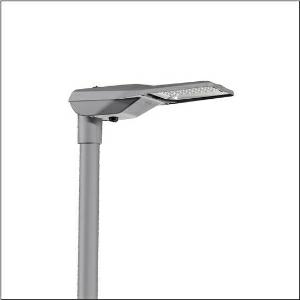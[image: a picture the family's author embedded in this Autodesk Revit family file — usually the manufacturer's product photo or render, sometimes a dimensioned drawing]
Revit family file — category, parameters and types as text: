
# Revit family: streetlight_sl_21_iq_mini___st1_0a_5xe2d61y08gb_62ef
name_source: partatom
category: Lighting Fixtures
units: mm (PartAtom-declared; Revit-internal decimal feet)

## family parameters
Cut with Voids When Loaded = No
Host = Face
Light Source = No
Part Type = Normal
Room Calculation Point = No
Round Connector Dimension = Use Diameter
Shared = No

## types (1)
- --- (1 x LED, 5200 lm, 39.8 W, 2700K)
    Apparent Load = 40 VA
    CIE Flux Codes = 37 72 97 100 100
    Color Rendering = 70
    Color Temperature = 2700K
    Default Elevation = 1800 mm
    Description = Streetlight SL 21 iQ mini, mast luminaire, primary light control with lens, of PMMA, primary optical cover: cover, of toughened safety glass, transparent, light distribution: ST1.0a, light emission: direct distribution, primary light characteristic: asymmetric, installation type: post-top, side-entry, LED, High Power LED, rated luminous flux: 5.200lm, luminous efficacy: 131lm/W, light colour: 727, colour temperature: 2700K, control gear: iQ-Street Remote, D4i with power reduction, control: pre-setting: logarithmic dimming characteristic, Street-Remote, Auto-Match, Temp-Guard, Lumen-Switch, Night-Set, Smart-Wire, Light-Fading, Desk-Remote (wireless, voltage-free reading and setting of iQ features in the workshop via application-optimized NFC function/RFID function), optimised constant luminous flux control (CLO 2.0), mains connection: 220..240V, AC, 50/60Hz, start of lifetime: 40W, end of service life: 41W, reduction: 18W, luminaire housing, of diecast aluminium, powder-coated, SITECO metallic grey (DB 702S), corrosivity category C5 high according to DIN EN ISO 12944, please order mast flange separately, inclination adjustable: 0°, 5°, 10°, 15°, sealing non-destructively replaceable, multi-level sealing system, length: 628mm, width: 235mm, height: 110mm, mast flange for spigot size: 42mm (side-entry): 5XC10008XM4, 60/48mm (side-entry/post-top): 5XC10108XM2, 76/60mm (side-entry/post-top): 5XC10108XM1, mounting height: 4..8m, Smart Interface below and above, protection rating (complete): IP66, insulation class (complete): insulation class II (safety insulation), certification: CE, ENEC, ENEC+, VDE, impact resistance: IK10, permissible operating ambient temperature for outdoor applications: -40..+50°C, standard-compliant lighting for roads and squares, packaging unit: 1 piece

Light Distribution: ST1.0a
    Height = 110 mm
    Lamp = 1 x LED
    Lamp Light Flux = 5200 lm
    Lamp Power = 39.8 W
    Lamp count = 1
    Length = 625 mm
    Luminous efficacy = 131 lm/W
    Manufacturer = Siteco
    ModVariant = No
    Model = 5XE2D61Y08GB
    Number of Poles = 1
    OnlyDefault = Yes
    Power Factor = 1
    Product Name = Streetlight SL 21 iQ mini | ST1.0a
    Product group = mast luminaire | pylon top
    ProductGroupID = 6100
    Protection Class = Protection class II
    Protection Degree = IP 66
    RLX_Detail_Level = 1
    RLX_Emergency_Light_Flux = 0 lm
    RLX_Emergency_Type = 0
    RLX_Emergency_Type_DB = No
    RlxData = <blob elided: 92793 chars, md5=2bfe383b>
    Socket = socket
    Standby Power = 0 W
    System Light Flux = 5200 lm
    System Power = 40 W
    Type Comments = factory setting: luminous flux: 100 % | dim-lin: 254 | 800 mA
    Type Image = l_1003514.jpg
    URL = http://relux.com
    VarID = @adj_115115
    Voltage = 0 V
    Weight = 0.00 kg
    Width = 234 mm

## geometry (parser evidence)
native form markers: Blend x4, Sweep x12
no freeform markers — native parametric forms only
